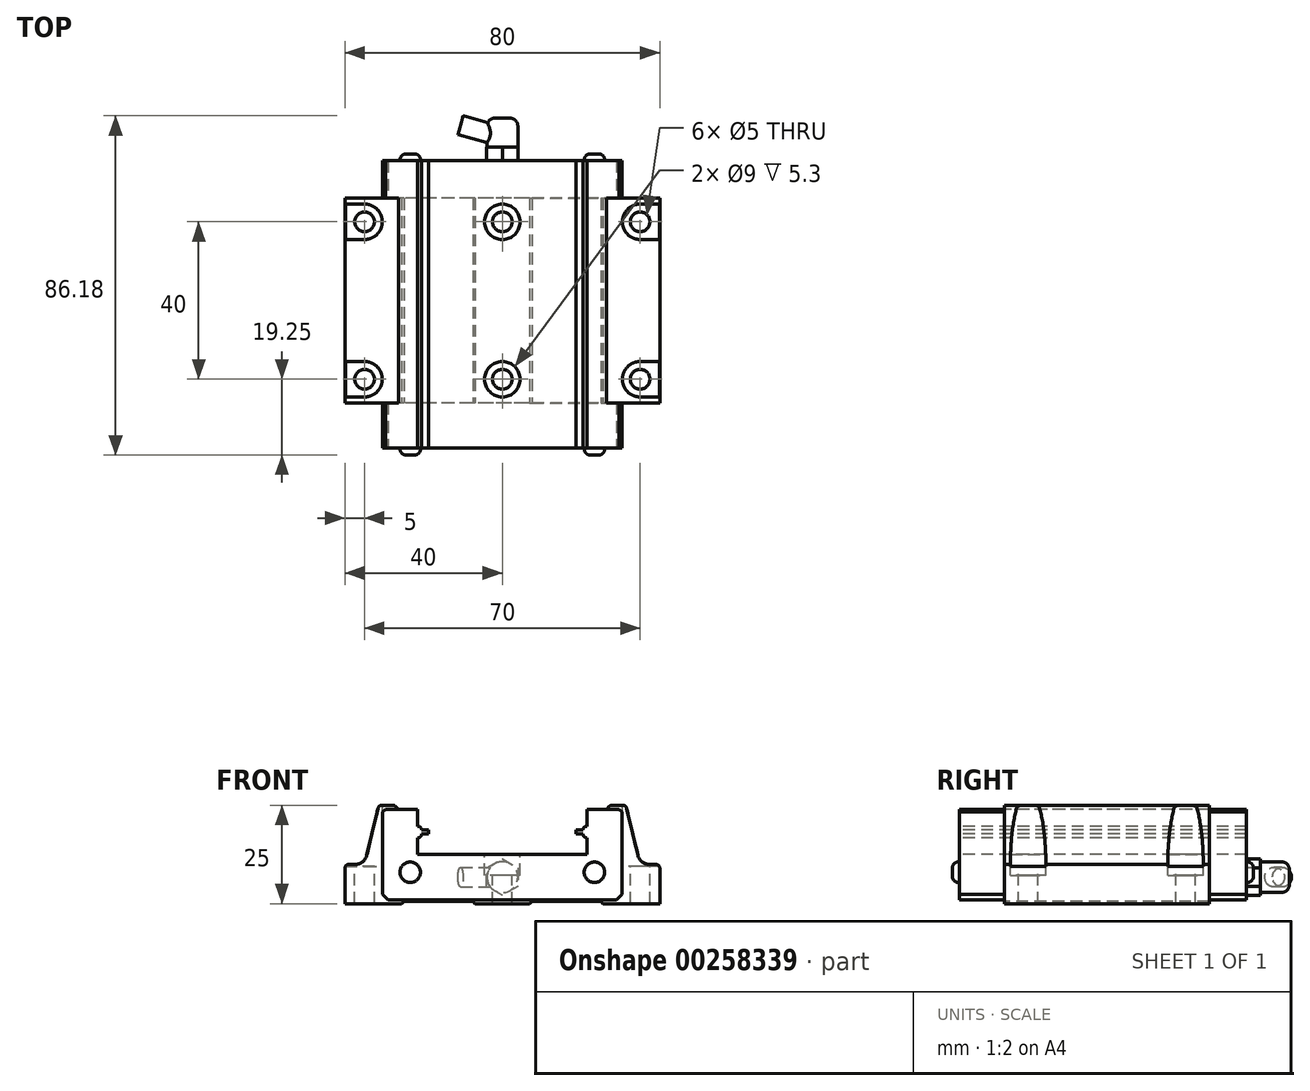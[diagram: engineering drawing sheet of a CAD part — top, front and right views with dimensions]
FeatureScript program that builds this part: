
annotation { "Feature Type Name" : "Feature", "Feature Type Description" : "" }
export const myFeature = defineFeature(function(context is Context, id is Id, definition is map)
    precondition{}
    {
        {
            var Q0;
            Q0=qCreatedBy(makeId("Front.planeOp"),FACE);
            var sketch = newSketch(context, id + "F0", { "sketchPlane" : qUnion([Q0])});
            skLineSegment(sketch, "E0", {"start": v(0, -7) * mm, "end": v(0, 7) * mm, "construction": true});
            skLineSegment(sketch, "E1", {"start": v(0, -7) * mm, "end": v(-21, -7) * mm});
            skLineSegment(sketch, "E2", {"start": v(-21, -7) * mm, "end": v(-21, -3.8) * mm});
            skLineSegment(sketch, "E3", {"start": v(-21, -3.8) * mm, "end": v(-21, -3.8) * mm});
            skLineSegment(sketch, "E4", {"start": v(-20, -2.8) * mm, "end": v(-20, -2.8) * mm});
            skLineSegment(sketch, "E5", {"start": v(-20, -2.8) * mm, "end": v(-18.2, -2.8) * mm});
            skLineSegment(sketch, "E6", {"start": v(-18.2, -2.8) * mm, "end": v(-18.2, -0.8) * mm});
            skLineSegment(sketch, "E7", {"start": v(-18.2, -0.8) * mm, "end": v(-20, -0.8) * mm});
            skLineSegment(sketch, "E8", {"start": v(-20, -0.8) * mm, "end": v(-20, -0.8) * mm});
            skLineSegment(sketch, "E9", {"start": v(-21, 0.2) * mm, "end": v(-21, 0.2) * mm});
            skLineSegment(sketch, "E10", {"start": v(-21, 0.2) * mm, "end": v(-21, 6.8) * mm});
            skLineSegment(sketch, "E11", {"start": v(-21, 6.8) * mm, "end": v(-20.3, 7.5) * mm});
            skLineSegment(sketch, "E12", {"start": v(-20.3, 7.5) * mm, "end": v(-6, 7.5) * mm});
            skLineSegment(sketch, "E13", {"start": v(-5.5, 7) * mm, "end": v(-6, 7.5) * mm});
            skLineSegment(sketch, "E14", {"start": v(-5.5, 7) * mm, "end": v(0, 7) * mm});
            skPoint(sketch, "E15.visualSharp", {"position": v(-20, -3.8) * mm});
            skArc(sketch, "E15.filletArc", {"start": v(-21, -3.8) * mm, "mid": v(-20.3, -3.5) * mm, "end": v(-20, -2.8) * mm});
            skPoint(sketch, "E16.visualSharp", {"position": v(-20, 0.2) * mm});
            skArc(sketch, "E16.filletArc", {"start": v(-20, -0.8) * mm, "mid": v(-20.3, -0.1) * mm, "end": v(-21, 0.2) * mm});
            skLineSegment(sketch, "E17", {"start": v(-18.2, -1.8) * mm, "end": v(-21, -1.8) * mm, "construction": true});
            skArc(sketch, "E18.MirrorCS", {"start": v(20, -0.8) * mm, "mid": v(20.3, -0.1) * mm, "end": v(21, 0.2) * mm});
            skArc(sketch, "E19.MirrorCS", {"start": v(21, -3.8) * mm, "mid": v(20.3, -3.5) * mm, "end": v(20, -2.8) * mm});
            skLineSegment(sketch, "E20.MirrorCS", {"start": v(5.5, 7) * mm, "end": v(6, 7.5) * mm});
            skLineSegment(sketch, "E21.MirrorCS", {"start": v(20, -2.8) * mm, "end": v(18.2, -2.8) * mm});
            skLineSegment(sketch, "E22.MirrorCS", {"start": v(18.2, -0.8) * mm, "end": v(20, -0.8) * mm});
            skLineSegment(sketch, "E23.MirrorCS", {"start": v(21, 6.8) * mm, "end": v(20.3, 7.5) * mm});
            skLineSegment(sketch, "E24.MirrorCS", {"start": v(18.2, -1.8) * mm, "end": v(21, -1.8) * mm, "construction": true});
            skLineSegment(sketch, "E25.MirrorCS", {"start": v(18.2, -2.8) * mm, "end": v(18.2, -0.8) * mm});
            skPoint(sketch, "E26.MirrorP", {"position": v(20, 0.2) * mm});
            skLineSegment(sketch, "E27.MirrorCS", {"start": v(0, -7) * mm, "end": v(21, -7) * mm});
            skPoint(sketch, "E28.MirrorP", {"position": v(20, -3.8) * mm});
            skLineSegment(sketch, "E29.MirrorCS", {"start": v(21, -7) * mm, "end": v(21, -3.8) * mm});
            skLineSegment(sketch, "E30.MirrorCS", {"start": v(5.5, 7) * mm, "end": v(0, 7) * mm});
            skLineSegment(sketch, "E31.MirrorCS", {"start": v(21, 0.2) * mm, "end": v(21, 0.2) * mm});
            skLineSegment(sketch, "E32.MirrorCS", {"start": v(21, -3.8) * mm, "end": v(21, -3.8) * mm});
            skLineSegment(sketch, "E33.MirrorCS", {"start": v(21, 0.2) * mm, "end": v(21, 6.8) * mm});
            skLineSegment(sketch, "E34.MirrorCS", {"start": v(20, -0.8) * mm, "end": v(20, -0.8) * mm});
            skLineSegment(sketch, "E35.MirrorCS", {"start": v(20.3, 7.5) * mm, "end": v(6, 7.5) * mm});
            skLineSegment(sketch, "E36.MirrorCS", {"start": v(20, -2.8) * mm, "end": v(20, -2.8) * mm});
            skSolve(sketch);
        }
        {
            var Q0;
            Q0=qCreatedBy(makeId("Front.planeOp"),FACE);
            var sketch = newSketch(context, id + "F1", { "sketchPlane" : qUnion([Q0])});
            skLineSegment(sketch, "E37", {"start": v(-21.5, 4) * mm, "end": v(-21.5, -0.3) * mm});
            skLineSegment(sketch, "E38", {"start": v(-21.5, -0.3) * mm, "end": v(-21.5, -0.3) * mm});
            skLineSegment(sketch, "E39", {"start": v(-20.5, -1.3) * mm, "end": v(-20.5, -1.3) * mm});
            skLineSegment(sketch, "E40", {"start": v(-20.5, -1.3) * mm, "end": v(-18.7, -1.3) * mm});
            skLineSegment(sketch, "E41", {"start": v(-18.7, -1.3) * mm, "end": v(-18.7, -2.3) * mm});
            skLineSegment(sketch, "E42", {"start": v(-18.7, -2.3) * mm, "end": v(-20.5, -2.3) * mm});
            skLineSegment(sketch, "E43", {"start": v(-20.5, -2.3) * mm, "end": v(-20.5, -2.3) * mm});
            skLineSegment(sketch, "E44", {"start": v(-21.5, -3.3) * mm, "end": v(-21.5, -3.3) * mm});
            skLineSegment(sketch, "E45", {"start": v(-21.5, -3.3) * mm, "end": v(-21.5, -7.5) * mm});
            skLineSegment(sketch, "E46", {"start": v(-21.5, -7.5) * mm, "end": v(0, -7.5) * mm});
            skLineSegment(sketch, "E47", {"start": v(0, -7.5) * mm, "end": v(0, -19) * mm, "construction": true});
            skLineSegment(sketch, "E48", {"start": v(0, -19) * mm, "end": v(-28.99, -19) * mm});
            skLineSegment(sketch, "E49", {"start": v(-30.4, -17.59) * mm, "end": v(-30.4, 3.3) * mm});
            skLineSegment(sketch, "E50", {"start": v(-30.4, 3.3) * mm, "end": v(-29.7, 4) * mm});
            skLineSegment(sketch, "E51", {"start": v(-29.7, 4) * mm, "end": v(-21.5, 4) * mm});
            skLineSegment(sketch, "E52", {"start": v(-28.99, -19) * mm, "end": v(-30.4, -17.59) * mm});
            skPoint(sketch, "E53.visualSharp", {"position": v(-20.5, -3.3) * mm});
            skArc(sketch, "E53.filletArc", {"start": v(-21.5, -3.3) * mm, "mid": v(-20.8, -3) * mm, "end": v(-20.5, -2.3) * mm});
            skPoint(sketch, "E54.visualSharp", {"position": v(-20.5, -0.3) * mm});
            skArc(sketch, "E54.filletArc", {"start": v(-20.5, -1.3) * mm, "mid": v(-20.8, -0.6) * mm, "end": v(-21.5, -0.3) * mm});
            skArc(sketch, "E55.MirrorCS", {"start": v(21.5, -3.3) * mm, "mid": v(20.8, -3) * mm, "end": v(20.5, -2.3) * mm});
            skLineSegment(sketch, "E56.MirrorCS", {"start": v(21.5, 4) * mm, "end": v(21.5, -0.3) * mm});
            skLineSegment(sketch, "E57.MirrorCS", {"start": v(18.7, -1.3) * mm, "end": v(18.7, -2.3) * mm});
            skLineSegment(sketch, "E58.MirrorCS", {"start": v(18.7, -2.3) * mm, "end": v(20.5, -2.3) * mm});
            skLineSegment(sketch, "E59.MirrorCS", {"start": v(20.5, -1.3) * mm, "end": v(18.7, -1.3) * mm});
            skArc(sketch, "E60.MirrorCS", {"start": v(20.5, -1.3) * mm, "mid": v(20.8, -0.6) * mm, "end": v(21.5, -0.3) * mm});
            skLineSegment(sketch, "E61.MirrorCS", {"start": v(28.99, -19) * mm, "end": v(30.4, -17.59) * mm});
            skLineSegment(sketch, "E62.MirrorCS", {"start": v(30.4, 3.3) * mm, "end": v(29.7, 4) * mm});
            skLineSegment(sketch, "E63.MirrorCS", {"start": v(20.5, -1.3) * mm, "end": v(20.5, -1.3) * mm});
            skLineSegment(sketch, "E64.MirrorCS", {"start": v(20.5, -2.3) * mm, "end": v(20.5, -2.3) * mm});
            skLineSegment(sketch, "E65.MirrorCS", {"start": v(21.5, -0.3) * mm, "end": v(21.5, -0.3) * mm});
            skLineSegment(sketch, "E66.MirrorCS", {"start": v(21.5, -3.3) * mm, "end": v(21.5, -7.5) * mm});
            skLineSegment(sketch, "E67.MirrorCS", {"start": v(30.4, -17.59) * mm, "end": v(30.4, 3.3) * mm});
            skLineSegment(sketch, "E68.MirrorCS", {"start": v(21.5, -3.3) * mm, "end": v(21.5, -3.3) * mm});
            skLineSegment(sketch, "E69.MirrorCS", {"start": v(29.7, 4) * mm, "end": v(21.5, 4) * mm});
            skLineSegment(sketch, "E70.MirrorCS", {"start": v(0, -19) * mm, "end": v(28.99, -19) * mm});
            skPoint(sketch, "E71.MirrorP", {"position": v(20.5, -3.3) * mm});
            skLineSegment(sketch, "E72.MirrorCS", {"start": v(21.5, -7.5) * mm, "end": v(0, -7.5) * mm});
            skPoint(sketch, "E73.MirrorP", {"position": v(20.5, -0.3) * mm});
            skSolve(sketch);
        }
        {
            var Q0;
            Q0=qSketchRegion(id+"F1",true);
            extrude(context, id + "F2", {"entities" : qUnion([Q0]), "oppositeDirection" : true, "depth" : 73 * mm});
        }
        {
            var Q0;
            Q0=qCreatedBy(makeId("Front.planeOp"),FACE);
            cPlane(context, id + "F3", {"entities" : qUnion([Q0]), "cplaneType" : CPlaneType.OFFSET, "offset" : 11.5 * mm, "oppositeDirection" : true, "width" : 150 * mm, "height" : 150 * mm});
        }
        {
            var Q0;
            Q0=qCreatedBy(id+"F3.planeOp",FACE);
            var sketch = newSketch(context, id + "F4", { "sketchPlane" : qUnion([Q0])});
            skLineSegment(sketch, "E74", {"start": v(0, 0) * mm, "end": v(0, -20) * mm, "construction": true});
            skLineSegment(sketch, "E75", {"start": v(0, -20) * mm, "end": v(-6.9, -20) * mm});
            skLineSegment(sketch, "E76", {"start": v(-6.9, -20) * mm, "end": v(-7.5, -19.4) * mm});
            skLineSegment(sketch, "E77", {"start": v(-7.5, -19.4) * mm, "end": v(-25, -19.4) * mm});
            skLineSegment(sketch, "E78", {"start": v(-25, -19.4) * mm, "end": v(-25.6, -20) * mm});
            skLineSegment(sketch, "E79", {"start": v(-25.6, -20) * mm, "end": v(-40, -20) * mm});
            skLineSegment(sketch, "E80", {"start": v(-40, -20) * mm, "end": v(-40, -11) * mm});
            skLineSegment(sketch, "E81", {"start": v(-39, -10) * mm, "end": v(-37.37, -10) * mm});
            skLineSegment(sketch, "E82", {"start": v(-34.45, -7.7) * mm, "end": v(-31.58, 4.23) * mm});
            skLineSegment(sketch, "E83", {"start": v(-30.61, 5) * mm, "end": v(-27.81, 5) * mm});
            skLineSegment(sketch, "E84", {"start": v(-27.1, 4.7) * mm, "end": v(-22.4, 0) * mm});
            skLineSegment(sketch, "E85", {"start": v(-22.4, 0) * mm, "end": v(-21.5, 0) * mm});
            skLineSegment(sketch, "E86", {"start": v(-21.5, 0) * mm, "end": v(-21.5, -7.5) * mm});
            skLineSegment(sketch, "E87", {"start": v(-21.5, -7.5) * mm, "end": v(0, -7.5) * mm});
            skPoint(sketch, "E88.visualSharp", {"position": v(-35, -10) * mm});
            skArc(sketch, "E88.filletArc", {"start": v(-37.37, -10) * mm, "mid": v(-35.5, -9.36) * mm, "end": v(-34.45, -7.7) * mm});
            skPoint(sketch, "E89.visualSharp", {"position": v(-31.4, 5) * mm});
            skArc(sketch, "E89.filletArc", {"start": v(-30.61, 5) * mm, "mid": v(-31.23, 4.79) * mm, "end": v(-31.58, 4.23) * mm});
            skPoint(sketch, "E90.visualSharp", {"position": v(-27.4, 5) * mm});
            skArc(sketch, "E90.filletArc", {"start": v(-27.1, 4.7) * mm, "mid": v(-27.43, 4.92) * mm, "end": v(-27.81, 5) * mm});
            skPoint(sketch, "E91.visualSharp", {"position": v(-40, -10) * mm});
            skArc(sketch, "E91.filletArc", {"start": v(-39, -10) * mm, "mid": v(-39.7, -10.3) * mm, "end": v(-40, -11) * mm});
            skArc(sketch, "E92.MirrorCS", {"start": v(27.1, 4.7) * mm, "mid": v(27.43, 4.92) * mm, "end": v(27.81, 5) * mm});
            skArc(sketch, "E93.MirrorCS", {"start": v(30.61, 5) * mm, "mid": v(31.23, 4.79) * mm, "end": v(31.58, 4.23) * mm});
            skArc(sketch, "E94.MirrorCS", {"start": v(39, -10) * mm, "mid": v(39.7, -10.3) * mm, "end": v(40, -11) * mm});
            skLineSegment(sketch, "E95.MirrorCS", {"start": v(39, -10) * mm, "end": v(37.37, -10) * mm});
            skLineSegment(sketch, "E96.MirrorCS", {"start": v(27.1, 4.7) * mm, "end": v(22.4, 0) * mm});
            skLineSegment(sketch, "E97.MirrorCS", {"start": v(30.61, 5) * mm, "end": v(27.81, 5) * mm});
            skLineSegment(sketch, "E98.MirrorCS", {"start": v(25, -19.4) * mm, "end": v(25.6, -20) * mm});
            skLineSegment(sketch, "E99.MirrorCS", {"start": v(6.9, -20) * mm, "end": v(7.5, -19.4) * mm});
            skArc(sketch, "E100.MirrorCS", {"start": v(37.37, -10) * mm, "mid": v(35.5, -9.36) * mm, "end": v(34.45, -7.7) * mm});
            skLineSegment(sketch, "E101.MirrorCS", {"start": v(34.45, -7.7) * mm, "end": v(31.58, 4.23) * mm});
            skLineSegment(sketch, "E102.MirrorCS", {"start": v(21.5, 0) * mm, "end": v(21.5, -7.5) * mm});
            skLineSegment(sketch, "E103.MirrorCS", {"start": v(40, -20) * mm, "end": v(40, -11) * mm});
            skLineSegment(sketch, "E104.MirrorCS", {"start": v(21.5, -7.5) * mm, "end": v(0, -7.5) * mm});
            skPoint(sketch, "E105.MirrorP", {"position": v(27.4, 5) * mm});
            skPoint(sketch, "E106.MirrorP", {"position": v(40, -10) * mm});
            skLineSegment(sketch, "E107.MirrorCS", {"start": v(22.4, 0) * mm, "end": v(21.5, 0) * mm});
            skPoint(sketch, "E108.MirrorP", {"position": v(35, -10) * mm});
            skLineSegment(sketch, "E109.MirrorCS", {"start": v(25.6, -20) * mm, "end": v(40, -20) * mm});
            skPoint(sketch, "E110.MirrorP", {"position": v(31.4, 5) * mm});
            skLineSegment(sketch, "E111.MirrorCS", {"start": v(7.5, -19.4) * mm, "end": v(25, -19.4) * mm});
            skLineSegment(sketch, "E112.MirrorCS", {"start": v(0, -20) * mm, "end": v(6.9, -20) * mm});
            skSolve(sketch);
        }
        {
            var Q0;
            Q0=qSketchRegion(id+"F4",true);
            extrude(context, id + "F5", {"entities" : qUnion([Q0]), "operationType" : NewBodyOperationType.ADD, "oppositeDirection" : true, "depth" : 52 * mm});
        }
        {
            var Q0;
            Q0=makeQuery(id+"F5.opExtrude","SWEPT_FACE",FACE,{"disambiguationData":[OSD([sQuery(id+"F4.wireOp",EDGE,"E79")])]});
            var sketch = newSketch(context, id + "F6", { "sketchPlane" : qUnion([Q0])});
            skLineSegment(sketch, "E113", {"start": v(0, 0) * mm, "end": v(0, -73) * mm, "construction": true});
            skPoint(sketch, "E114", {"position": v(-35, -17.5) * mm});
            skPoint(sketch, "E115", {"position": v(-35, -57.5) * mm});
            skPoint(sketch, "E116", {"position": v(0, -17.5) * mm});
            skPoint(sketch, "E117", {"position": v(0, -57.5) * mm});
            skPoint(sketch, "E118", {"position": v(35, -17.5) * mm});
            skPoint(sketch, "E119", {"position": v(35, -57.5) * mm});
            skLineSegment(sketch, "E120", {"start": v(-40, -37.5) * mm, "end": v(40, -37.5) * mm, "construction": true});
            skLineSegment(sketch, "E121", {"start": v(-35, -17.5) * mm, "end": v(35, -17.5) * mm, "construction": true});
            skLineSegment(sketch, "E122", {"start": v(-35, -57.5) * mm, "end": v(35, -57.5) * mm, "construction": true});
            skSolve(sketch);
        }
        {
            var Q0;
            Q0=sQuery(id+"F6.wireOp",VERTEX,"E114");
            var Q1;
            Q1=sQuery(id+"F6.wireOp",VERTEX,"E115");
            var Q2;
            Q2=sQuery(id+"F6.wireOp",VERTEX,"E116");
            var Q3;
            Q3=sQuery(id+"F6.wireOp",VERTEX,"E117");
            var Q4;
            Q4=sQuery(id+"F6.wireOp",VERTEX,"E118");
            var Q5;
            Q5=sQuery(id+"F6.wireOp",VERTEX,"E119");
            var Q6;
            Q6=makeQuery(id+"F2.opExtrude","SWEPT_BODY",BODY,{"disambiguationData":[OSD([sQuery(id+"F1.wireOp",EDGE,"E37"),sQuery(id+"F1.wireOp",EDGE,"E40"),sQuery(id+"F1.wireOp",EDGE,"E41"),sQuery(id+"F1.wireOp",EDGE,"E42"),sQuery(id+"F1.wireOp",EDGE,"E45"),sQuery(id+"F1.wireOp",EDGE,"E46"),sQuery(id+"F1.wireOp",EDGE,"E48"),sQuery(id+"F1.wireOp",EDGE,"E49"),sQuery(id+"F1.wireOp",EDGE,"E50"),sQuery(id+"F1.wireOp",EDGE,"E51"),sQuery(id+"F1.wireOp",EDGE,"E52"),sQuery(id+"F1.wireOp",EDGE,"E53.filletArc"),sQuery(id+"F1.wireOp",EDGE,"E54.filletArc"),sQuery(id+"F1.wireOp",EDGE,"E55.MirrorCS"),sQuery(id+"F1.wireOp",EDGE,"E56.MirrorCS"),sQuery(id+"F1.wireOp",EDGE,"E57.MirrorCS"),sQuery(id+"F1.wireOp",EDGE,"E58.MirrorCS"),sQuery(id+"F1.wireOp",EDGE,"E59.MirrorCS"),sQuery(id+"F1.wireOp",EDGE,"E60.MirrorCS"),sQuery(id+"F1.wireOp",EDGE,"E61.MirrorCS"),sQuery(id+"F1.wireOp",EDGE,"E62.MirrorCS"),sQuery(id+"F1.wireOp",EDGE,"E66.MirrorCS"),sQuery(id+"F1.wireOp",EDGE,"E67.MirrorCS"),sQuery(id+"F1.wireOp",EDGE,"E69.MirrorCS"),sQuery(id+"F1.wireOp",EDGE,"E70.MirrorCS"),sQuery(id+"F1.wireOp",EDGE,"E72.MirrorCS")])]});
            hole(context, id + "F7", {"style" : HoleStyle.SIMPLE, "endStyle" : HoleEndStyle.THROUGH, "standardTappedOrClearance" : lookupTablePath({ "standard" : "ISO", "engagement" : "75%", "pitch" : "1 mm", "size" : "M6", "type" : "Tapped" }), "standardBlindInLast" : lookupTablePath({ "standard" : "ISO", "engagement" : "75%", "pitch" : "1 mm", "size" : "M6", "type" : "Tapped" }), "holeDiameter" : 5 * mm, "locations" : qUnion([Q0, Q1, Q2, Q3, Q4, Q5]), "scope" : qUnion([Q6]), "isTappedThrough" : true, "majorDiameter" : 6 * mm, "showTappedDepth" : true, "startStyle" : HoleStartStyle.PART});
        }
        {
            var Q0;
            Q0=makeQuery(id+"F5.opExtrude","SWEPT_FACE",FACE,{"disambiguationData":[OSD([sQuery(id+"F4.wireOp",EDGE,"E81")])]});
            var sketch = newSketch(context, id + "F8", { "sketchPlane" : qUnion([Q0])});
            skArc(sketch, "E123", {"start": v(-35, 53) * mm, "mid": v(-30.5, 57.5) * mm, "end": v(-35, 62) * mm});
            skLineSegment(sketch, "E124", {"start": v(-35, 62) * mm, "end": v(-40, 62) * mm});
            skLineSegment(sketch, "E125", {"start": v(-40, 62) * mm, "end": v(-40, 53) * mm});
            skLineSegment(sketch, "E126", {"start": v(-40, 53) * mm, "end": v(-35, 53) * mm});
            skLineSegment(sketch, "E127", {"start": v(-39, 37.5) * mm, "end": v(40, 37.5) * mm, "construction": true});
            skPoint(sketch, "E127.endSnap0", {"position": v(-39, 37.5) * mm});
            skLineSegment(sketch, "E128.MirrorCS", {"start": v(-40, 22) * mm, "end": v(-35, 22) * mm});
            skLineSegment(sketch, "E129.MirrorCS", {"start": v(-40, 13) * mm, "end": v(-40, 22) * mm});
            skArc(sketch, "E130.MirrorCS", {"start": v(-35, 22) * mm, "mid": v(-30.5, 17.5) * mm, "end": v(-35, 13) * mm});
            skLineSegment(sketch, "E131.MirrorCS", {"start": v(-35, 13) * mm, "end": v(-40, 13) * mm});
            skArc(sketch, "E132.MirrorCS", {"start": v(35, 22) * mm, "mid": v(30.5, 17.5) * mm, "end": v(35, 13) * mm});
            skLineSegment(sketch, "E133.MirrorCS", {"start": v(40, 13) * mm, "end": v(40, 22) * mm});
            skLineSegment(sketch, "E134.MirrorCS", {"start": v(40, 22) * mm, "end": v(35, 22) * mm});
            skLineSegment(sketch, "E135.MirrorCS", {"start": v(40, 53) * mm, "end": v(35, 53) * mm});
            skLineSegment(sketch, "E136.MirrorCS", {"start": v(40, 62) * mm, "end": v(40, 53) * mm});
            skLineSegment(sketch, "E137.MirrorCS", {"start": v(35, 62) * mm, "end": v(40, 62) * mm});
            skArc(sketch, "E138.MirrorCS", {"start": v(35, 53) * mm, "mid": v(30.5, 57.5) * mm, "end": v(35, 62) * mm});
            skLineSegment(sketch, "E139.MirrorCS", {"start": v(35, 13) * mm, "end": v(40, 13) * mm});
            skPoint(sketch, "E140.MirrorP", {"position": v(39, 37.5) * mm});
            skSolve(sketch);
        }
        {
            var Q0;
            Q0=qSketchRegion(id+"F8",true);
            extrude(context, id + "F9", {"entities" : qUnion([Q0]), "operationType" : NewBodyOperationType.REMOVE, "oppositeDirection" : true, "depth" : 0.5 * mm, "hasSecondDirection" : true, "secondDirectionBound" : BoundingType.THROUGH_ALL, "secondDirectionOppositeDirection" : false, "secondDirectionDepth" : 25 * mm});
        }
        {
            var Q0;
            Q0=makeQuery(id+"F2.opExtrude","SWEPT_FACE",FACE,{"disambiguationData":[OSD([sQuery(id+"F1.wireOp",EDGE,"E46"),sQuery(id+"F1.wireOp",EDGE,"E72.MirrorCS")])]});
            var sketch = newSketch(context, id + "F10", { "sketchPlane" : qUnion([Q0])});
            skCircle(sketch, "E141", {"center": v(0, 57.5) * mm, "radius": 4.5 * mm});
            skCircle(sketch, "E142", {"center": v(0, 17.5) * mm, "radius": 4.5 * mm});
            skSolve(sketch);
        }
        {
            var Q0;
            Q0=qSketchRegion(id+"F10",true);
            extrude(context, id + "F11", {"entities" : qUnion([Q0]), "operationType" : NewBodyOperationType.REMOVE, "oppositeDirection" : true, "depth" : 5.3 * mm});
        }
        {
            var Q0;
            Q0=makeQuery(id+"F2.opExtrude","CAP_FACE",FACE,{"disambiguationData":[OSD([sQuery(id+"F1.wireOp",EDGE,"E37"),sQuery(id+"F1.wireOp",EDGE,"E40"),sQuery(id+"F1.wireOp",EDGE,"E41"),sQuery(id+"F1.wireOp",EDGE,"E42"),sQuery(id+"F1.wireOp",EDGE,"E45"),sQuery(id+"F1.wireOp",EDGE,"E46"),sQuery(id+"F1.wireOp",EDGE,"E48"),sQuery(id+"F1.wireOp",EDGE,"E49"),sQuery(id+"F1.wireOp",EDGE,"E50"),sQuery(id+"F1.wireOp",EDGE,"E51"),sQuery(id+"F1.wireOp",EDGE,"E52"),sQuery(id+"F1.wireOp",EDGE,"E53.filletArc"),sQuery(id+"F1.wireOp",EDGE,"E54.filletArc"),sQuery(id+"F1.wireOp",EDGE,"E55.MirrorCS"),sQuery(id+"F1.wireOp",EDGE,"E56.MirrorCS"),sQuery(id+"F1.wireOp",EDGE,"E57.MirrorCS"),sQuery(id+"F1.wireOp",EDGE,"E58.MirrorCS"),sQuery(id+"F1.wireOp",EDGE,"E59.MirrorCS"),sQuery(id+"F1.wireOp",EDGE,"E60.MirrorCS"),sQuery(id+"F1.wireOp",EDGE,"E61.MirrorCS"),sQuery(id+"F1.wireOp",EDGE,"E62.MirrorCS"),sQuery(id+"F1.wireOp",EDGE,"E66.MirrorCS"),sQuery(id+"F1.wireOp",EDGE,"E67.MirrorCS"),sQuery(id+"F1.wireOp",EDGE,"E69.MirrorCS"),sQuery(id+"F1.wireOp",EDGE,"E70.MirrorCS"),sQuery(id+"F1.wireOp",EDGE,"E72.MirrorCS")])],"isStart":true});
            var sketch = newSketch(context, id + "F12", { "sketchPlane" : qUnion([Q0])});
            skLineSegment(sketch, "E143", {"start": v(0, 0) * mm, "end": v(0, -19) * mm, "construction": true});
            skCircle(sketch, "E144", {"center": v(-23.4, -12) * mm, "radius": 2.6 * mm});
            skCircle(sketch, "E145", {"center": v(23.4, -12) * mm, "radius": 2.6 * mm});
            skSolve(sketch);
        }
        {
            var Q0;
            Q0=qSketchRegion(id+"F12",true);
            extrude(context, id + "F13", {"entities" : qUnion([Q0]), "depth" : 1.75 * mm});
        }
        {
            var Q0;
            Q0=makeQuery(id+"F13.opExtrude","CAP_FACE",FACE,{"disambiguationData":[OSD([sQuery(id+"F12.wireOp",EDGE,"E144")])],"isStart":false});
            var Q1;
            Q1=makeQuery(id+"F13.opExtrude","CAP_FACE",FACE,{"disambiguationData":[OSD([sQuery(id+"F12.wireOp",EDGE,"E145")])],"isStart":false});
            fillet(context, id + "F14", {"entities" : qUnion([Q0, Q1]), "radius" : 1.5 * mm, "tangentPropagation" : true, "allowEdgeOverflow" : false});
        }
        {
            var Q0;
            Q0=makeQuery(id+"F2.opExtrude","CAP_FACE",FACE,{"disambiguationData":[OSD([sQuery(id+"F1.wireOp",EDGE,"E37"),sQuery(id+"F1.wireOp",EDGE,"E40"),sQuery(id+"F1.wireOp",EDGE,"E41"),sQuery(id+"F1.wireOp",EDGE,"E42"),sQuery(id+"F1.wireOp",EDGE,"E45"),sQuery(id+"F1.wireOp",EDGE,"E46"),sQuery(id+"F1.wireOp",EDGE,"E48"),sQuery(id+"F1.wireOp",EDGE,"E49"),sQuery(id+"F1.wireOp",EDGE,"E50"),sQuery(id+"F1.wireOp",EDGE,"E51"),sQuery(id+"F1.wireOp",EDGE,"E52"),sQuery(id+"F1.wireOp",EDGE,"E53.filletArc"),sQuery(id+"F1.wireOp",EDGE,"E54.filletArc"),sQuery(id+"F1.wireOp",EDGE,"E55.MirrorCS"),sQuery(id+"F1.wireOp",EDGE,"E56.MirrorCS"),sQuery(id+"F1.wireOp",EDGE,"E57.MirrorCS"),sQuery(id+"F1.wireOp",EDGE,"E58.MirrorCS"),sQuery(id+"F1.wireOp",EDGE,"E59.MirrorCS"),sQuery(id+"F1.wireOp",EDGE,"E60.MirrorCS"),sQuery(id+"F1.wireOp",EDGE,"E61.MirrorCS"),sQuery(id+"F1.wireOp",EDGE,"E62.MirrorCS"),sQuery(id+"F1.wireOp",EDGE,"E66.MirrorCS"),sQuery(id+"F1.wireOp",EDGE,"E67.MirrorCS"),sQuery(id+"F1.wireOp",EDGE,"E69.MirrorCS"),sQuery(id+"F1.wireOp",EDGE,"E70.MirrorCS"),sQuery(id+"F1.wireOp",EDGE,"E72.MirrorCS")])],"isStart":false});
            var sketch = newSketch(context, id + "F15", { "sketchPlane" : qUnion([Q0])});
            skLineSegment(sketch, "E146", {"start": v(0, -7.5) * mm, "end": v(0, -19) * mm, "construction": true});
            skCircle(sketch, "E147", {"center": v(0, -13.25) * mm, "radius": 4.62 * mm, "construction": true});
            skLineSegment(sketch, "E148", {"start": v(0, -8.63) * mm, "end": v(-4, -10.94) * mm});
            skLineSegment(sketch, "E149", {"start": v(-4, -10.94) * mm, "end": v(-4, -15.56) * mm});
            skLineSegment(sketch, "E150", {"start": v(-4, -15.56) * mm, "end": v(0, -17.87) * mm});
            skLineSegment(sketch, "E151", {"start": v(0, -17.87) * mm, "end": v(4, -15.56) * mm});
            skLineSegment(sketch, "E152", {"start": v(4, -15.56) * mm, "end": v(4, -10.94) * mm});
            skLineSegment(sketch, "E153", {"start": v(4, -10.94) * mm, "end": v(0, -8.63) * mm});
            skSolve(sketch);
        }
        {
            var Q0;
            Q0=qSketchRegion(id+"F15",true);
            extrude(context, id + "F16", {"entities" : qUnion([Q0]), "operationType" : NewBodyOperationType.ADD, "depth" : 3.5 * mm});
        }
        {
            var Q0;
            Q0=makeQuery(id+"F16.opExtrude","CAP_FACE",FACE,{"disambiguationData":[OSD([sQuery(id+"F15.wireOp",EDGE,"E148"),sQuery(id+"F15.wireOp",EDGE,"E149"),sQuery(id+"F15.wireOp",EDGE,"E150"),sQuery(id+"F15.wireOp",EDGE,"E151"),sQuery(id+"F15.wireOp",EDGE,"E152"),sQuery(id+"F15.wireOp",EDGE,"E153")])],"isStart":false});
            var sketch = newSketch(context, id + "F17", { "sketchPlane" : qUnion([Q0])});
            skPoint(sketch, "E154", {"position": v(0, -13.25) * mm});
            skCircle(sketch, "E155", {"center": v(0, -13.25) * mm, "radius": 3.92 * mm});
            skSolve(sketch);
        }
        {
            var Q0;
            Q0=qSketchRegion(id+"F17",true);
            extrude(context, id + "F18", {"entities" : qUnion([Q0]), "operationType" : NewBodyOperationType.ADD, "depth" : 7.35 * mm});
        }
        {
            var Q0;
            Q0=makeQuery(id+"F18.opExtrude","CAP_FACE",FACE,{"disambiguationData":[OSD([sQuery(id+"F17.wireOp",EDGE,"E155")])],"isStart":false});
            fillet(context, id + "F19", {"entities" : qUnion([Q0]), "radius" : 2 * mm, "tangentPropagation" : true, "allowEdgeOverflow" : false});
        }
        {
            var Q0;
            Q0=qCreatedBy(makeId("Right.planeOp"),FACE);
            var sketch = newSketch(context, id + "F20", { "sketchPlane" : qUnion([Q0])});
            skLineSegment(sketch, "E156", {"start": v(79.17, -8) * mm, "end": v(79.17, -18.1) * mm, "construction": true});
            skSolve(sketch);
        }
        {
            var Q0;
            Q0=sQuery(id+"F20.wireOp",EDGE,"E156");
            cPlane(context, id + "F21", {"entities" : qUnion([Q0]), "cplaneType" : CPlaneType.LINE_ANGLE, "offset" : 25 * mm, "angle" : 15 * degree, "width" : 150 * mm, "height" : 150 * mm});
        }
        {
            var Q0;
            Q0=qCreatedBy(id+"F21.planeOp",FACE);
            var sketch = newSketch(context, id + "F22", { "sketchPlane" : qUnion([Q0])});
            skLineSegment(sketch, "E157", {"start": v(-80.5, -13.25) * mm, "end": v(-70.51, -13.25) * mm, "construction": true});
            skPoint(sketch, "E158", {"position": v(-76.47, -13.25) * mm});
            skCircle(sketch, "E159", {"center": v(-76.47, -13.25) * mm, "radius": 2.5 * mm});
            skSolve(sketch);
        }
        {
            var Q0;
            Q0=qSketchRegion(id+"F22",true);
            extrude(context, id + "F23", {"entities" : qUnion([Q0]), "operationType" : NewBodyOperationType.ADD, "depth" : 11 * mm});
        }
        {
            var Q0;
            Q0=makeQuery(id+"F2.opExtrude","SWEPT_EDGE",EDGE,{"disambiguationData":[OSD([sQuery(id+"F1.wireOp",EDGE,"E40"),sQuery(id+"F1.wireOp",EDGE,"E54.filletArc")])]});
            cPoint(context, id + "F24", {"entities" : qUnion([Q0]), "parameter" : 0.5});
        }
        {
            var Q0;
            Q0=qCreatedBy(makeId("Front.planeOp"),FACE);
            var Q1;
            Q1=qCreatedBy(id+"F24",VERTEX);
            cPlane(context, id + "F25", {"entities" : qUnion([Q0, Q1]), "cplaneType" : CPlaneType.PLANE_POINT, "offset" : 25 * mm, "width" : 150 * mm, "height" : 150 * mm});
        }
        {
            var Q0;
            Q0=makeQuery(id+"F13.opExtrude","SWEPT_BODY",BODY,{"disambiguationData":[OSD([sQuery(id+"F12.wireOp",EDGE,"E144")])]});
            var Q1;
            Q1=makeQuery(id+"F13.opExtrude","SWEPT_BODY",BODY,{"disambiguationData":[OSD([sQuery(id+"F12.wireOp",EDGE,"E145")])]});
            var Q2;
            Q2=qCreatedBy(id+"F25.planeOp",FACE);
            mirror(context, id + "F26", {"operationType" : NewBodyOperationType.ADD, "entities" : qUnion([Q0, Q1]), "mirrorPlane" : qUnion([Q2])});
        }
    });
